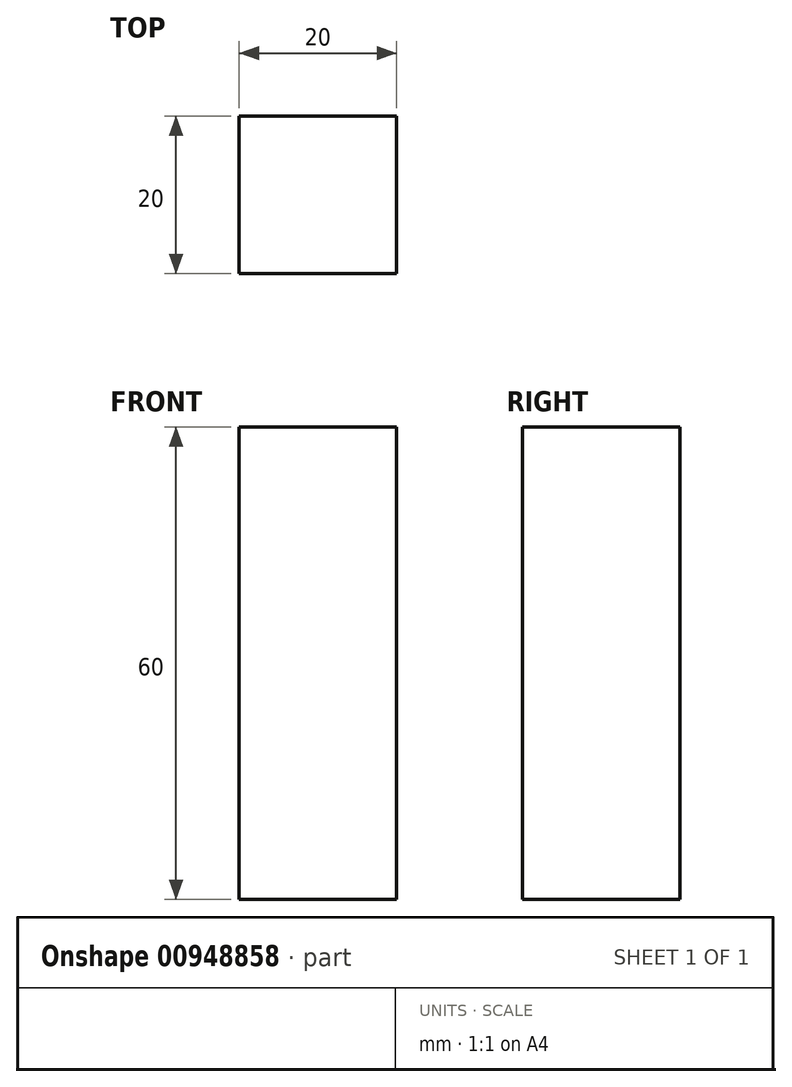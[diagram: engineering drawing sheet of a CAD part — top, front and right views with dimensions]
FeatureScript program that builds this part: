
annotation { "Feature Type Name" : "Feature", "Feature Type Description" : "" }
export const myFeature = defineFeature(function(context is Context, id is Id, definition is map)
    precondition{}
    {
        {
            var Q0;
            Q0=qCreatedBy(makeId("Top.planeOp"),FACE);
            var sketch = newSketch(context, id + "F0", { "sketchPlane" : qUnion([Q0])});
            skLineSegment(sketch, "E0.bottom", {"start": v(-10, 10) * mm, "end": v(10, 10) * mm});
            skLineSegment(sketch, "E0.top", {"start": v(-10, -10) * mm, "end": v(10, -10) * mm});
            skLineSegment(sketch, "E0.left", {"start": v(-10, 10) * mm, "end": v(-10, -10) * mm});
            skLineSegment(sketch, "E0.right", {"start": v(10, 10) * mm, "end": v(10, -10) * mm});
            skSolve(sketch);
        }
        {
            var Q0;
            Q0=makeQuery(id+"F0.imprint","IMPRINT",FACE,{"disambiguationData":[TD([[makeQuery(id+"F0.imprint","IMPRINT",EDGE,{"derivedFrom":sQuery(id+"F0.wireOp",EDGE,"E0.bottom")}),-1.0]])]});
            extrude(context, id + "F1", {"entities" : qUnion([Q0]), "depth" : 60 * mm, "offsetDistance" : 25 * mm});
        }
    });
